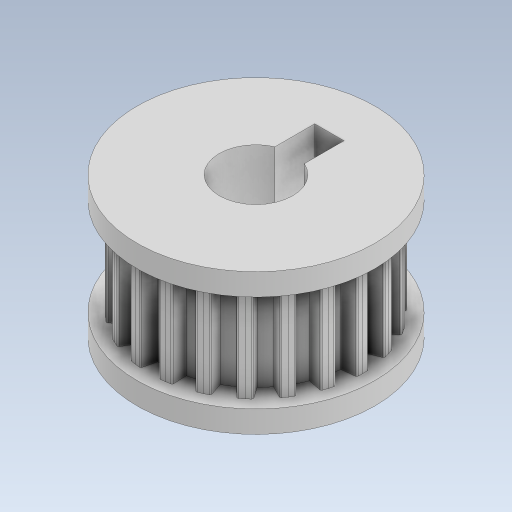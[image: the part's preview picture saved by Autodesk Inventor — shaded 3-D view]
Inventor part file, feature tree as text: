
AUTODESK INVENTOR PART (.ipt)
format: ipt  version: 2023.5 (Build 275446000, 446)  size: 824,832 bytes
history: native  units: mm
features: extrude x5, sketch x4, projected_geometry x3, pattern_circular x1
ambient origin geometry x8: Origin, YZ Plane, XZ Plane, XY Plane, X Axis, Y Axis, Z Axis, Center Point
bodies: Solid1 (feature_tree)
feature tree (13):
  sketch  "Sketch1"  dims[d0=5.0mm d2=14.55mm]
  extrude  "Extrusion1"  Depth=14.55mm
  extrude  "Extrusion2"  Depth=0.4mm
  pattern_circular  "Circular Pattern1"  [2 undecoded]
  extrude  "Extrusion3"  Depth=10.0mm TaperAngle=360.0deg
  extrude  "Extrusion4"  Depth=10.0mm
  extrude  "Extrusion6"  Depth=1.5mm TaperAngle=0.0deg
  sketch  "Sketch2"  dims[d3=12.6mm d4=0.4mm]
  sketch  "Sketch3"  dims[d5=0.1mm]
  sketch  "Sketch5"  dims[d6=6.6mm d7=0.0mm d8=6.6mm d9=0.0mm d10=220.0mm d11=360.0deg d13=16.2mm d14=1.5mm d15=0.0mm d16=1.5mm d17=0.0mm d20=16.2mm d21=5.0mm d22=5.0mm d23=5.0mm d24=10.0mm d25=0.0mm d26=14.55mm d18=0.5mm d19=0.872665mm]
  projected_geometry  "Projected Loop1"
  projected_geometry  "Projected Loop2"
  projected_geometry  "Projected Loop3"
note: 2 required parameter values undecoded (feature->parameter linkage not recoverable at this tier; creation-order binding heuristic only, values carry confidence <= 0.55)
